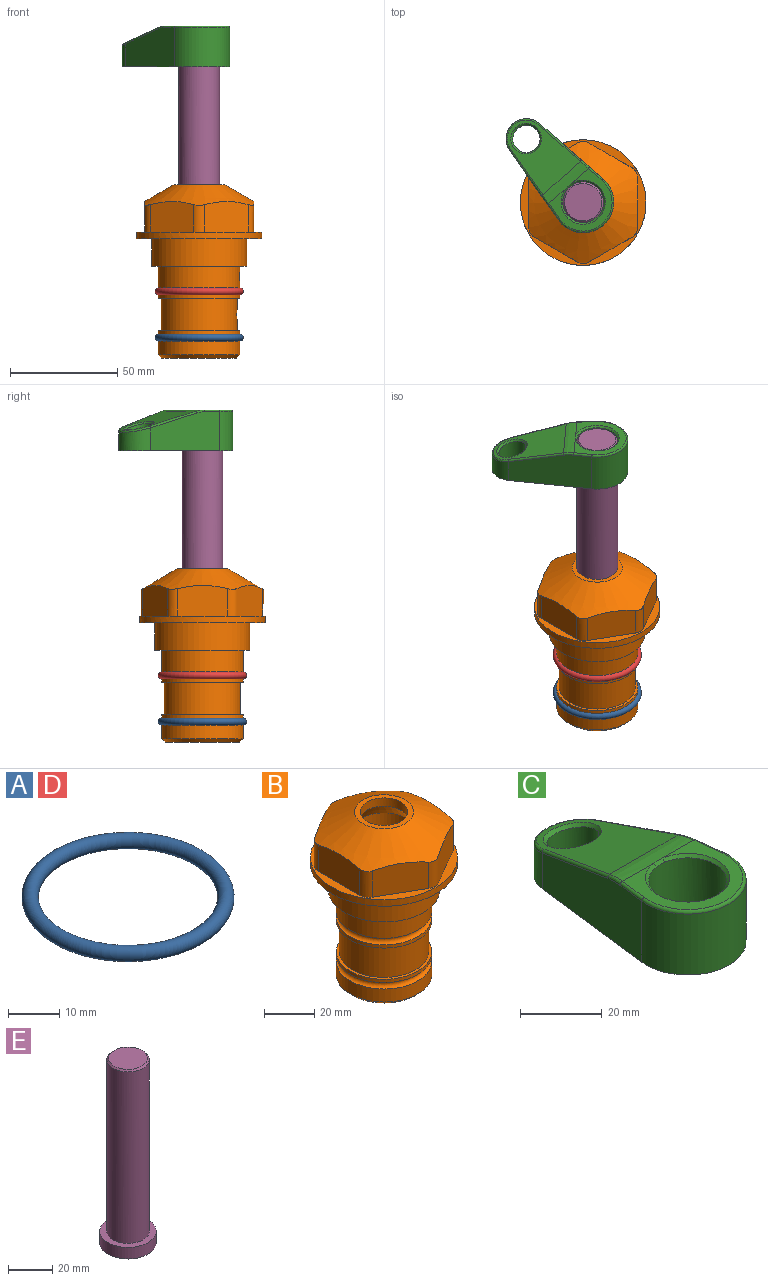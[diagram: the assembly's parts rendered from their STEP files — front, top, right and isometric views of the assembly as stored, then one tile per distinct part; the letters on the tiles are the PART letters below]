
ASSEMBLY  parts=5 mates=4
PART A: 1 faces, bbox 44.7x44.7x3.2 mm
  f0: torus R=19.05mm, axis (0,0,1), area 1193.9mm2
PART B: 36 faces, bbox 58.7x58.7x81 mm
  f0: cylinder r=17.78mm len=35.56mm, axis (0,0,1), area 1670.8mm2, adj f23,f24,f31
  f1: cylinder r=19.05mm len=38.1mm, axis (0,0,1), area 1191.9mm2, adj f26,f27,f30
  f2: plane 58.66x58.66mm, normal (0,0,-1), area 1150.6mm2, adj f3,f28
  f3: cylinder r=29.33mm len=58.66mm, axis (0,0,-1), area 585.1mm2, adj f2,f4
  f4: plane 58.66x58.66mm, normal (0,0,1), area 475.9mm2, adj f3,f5,f6,f7,f8,f9,f10,f11
  f5: plane 20.32x14.34mm, normal (-0.5,0.87,0), area 324.4mm2, adj f4,f15,f16,f17
  f6: plane 20.32x14.34mm, normal (0.5,0.87,0), area 324.4mm2, adj f4,f14,f15,f17
  f7: plane 23.48x14.34mm, normal (1,0,0), area 324.4mm2, adj f4,f13,f14,f17
  f8: plane 20.32x14.34mm, normal (0.5,-0.87,0), area 324.4mm2, adj f4,f12,f13,f17
  f9: plane 20.32x14.34mm, normal (-0.5,-0.87,0), area 324.4mm2, adj f4,f11,f12,f17
  f10: plane 23.48x14.34mm, normal (-1,0,0), area 324.4mm2, adj f4,f11,f16,f17
  f11: cylinder r=5.08mm len=12.85mm, axis (0,0,-1), area 67.2mm2, adj f4,f9,f10,f17
  f12: cylinder r=5.08mm len=12.85mm, axis (0,0,-1), area 67.2mm2, adj f4,f8,f9,f17
  f13: cylinder r=5.08mm len=12.85mm, axis (0,0,-1), area 67.2mm2, adj f4,f7,f8,f17
  f14: cylinder r=5.08mm len=12.85mm, axis (0,0,-1), area 67.2mm2, adj f4,f6,f7,f17
  f15: cylinder r=5.08mm len=12.85mm, axis (0,0,-1), area 67.2mm2, adj f4,f5,f6,f17
  f16: cylinder r=5.08mm len=12.85mm, axis (0,0,-1), area 67.2mm2, adj f4,f5,f10,f17
  f17: cone r=11.73mm half-angle=60deg, axis (0,0,-1), area 2071.8mm2, adj f5,f6,f7,f8,f9,f10,f11,f12
  f18: plane 23.46x23.46mm, normal (0,0,1), area 147.4mm2, adj f17,f35
  f19: plane 34.93x34.93mm, normal (0,0,-1), area 958mm2, adj f29
  f20: cylinder r=19.05mm len=38.1mm, axis (0,0,1), area 760.1mm2, adj f21,f29
  f21: torus R=19.05mm, axis (0,0,1), area 565.3mm2, adj f20,f22
  f22: cylinder r=19.05mm len=38.1mm, axis (0,0,1), area 190mm2, adj f21,f23
  f23: plane 38.1x38.1mm, normal (0,0,1), area 146.9mm2, adj f0,f22
  f24: plane 38.1x38.1mm, normal (0,0,-1), area 146.9mm2, adj f0,f25
  f25: cylinder r=19.05mm len=38.1mm, axis (0,0,1), area 190mm2, adj f24,f26
  f26: torus R=19.05mm, axis (0,0,1), area 565.3mm2, adj f1,f25
  f27: plane 44.45x44.45mm, normal (0,0,-1), area 411.7mm2, adj f1,f28
  f28: cylinder r=22.23mm len=44.45mm, axis (0,0,1), area 1773.5mm2, adj f2,f27
  f29: cone r=19.05mm half-angle=45deg, axis (0,0,1), area 257.5mm2, adj f19,f20
  f30: cylinder r=3.17mm len=6.75mm, axis (-1,0,0), area 128mm2, adj f1,f33
  f31: cylinder r=3.17mm len=6.35mm, axis (-1,0,0), area 102.5mm2, adj f0,f33
  f32: plane 25.4x25.4mm, normal (0,0,1), area 506.7mm2, adj f33
  f33: cylinder r=12.7mm len=66.42mm, axis (0,0,-1), area 5236.2mm2, adj f30,f31,f32,f34
  f34: cone r=9.53mm half-angle=30deg, axis (0,0,-1), area 443.4mm2, adj f33,f35
  f35: cylinder r=9.53mm len=19.05mm, axis (0,0,-1), area 240.9mm2, adj f18,f34
PART C: 31 faces, bbox 31.7x65.5x19.8 mm
  f0: plane 39.12x18.26mm, normal (0.99,0.12,0), area 612.2mm2, adj f1,f4,f7,f11,f13,f15
  f1: cylinder r=9.53mm len=18.91mm, axis (0,0,-1), area 296.1mm2, adj f0,f2,f7,f17
  f2: plane 39.12x18.26mm, normal (-0.99,0.12,0), area 612.2mm2, adj f1,f4,f7,f12,f14,f16
  f3: cylinder r=6.35mm len=12.7mm, axis (0,0,-1), area 362.4mm2, adj f7,f18
  f4: cylinder r=14.29mm len=28.58mm, axis (0,0,-1), area 882.2mm2, adj f0,f2,f7,f10
  f5: cylinder r=9.53mm len=19.05mm, axis (0,0,-1), area 1092.6mm2, adj f7,f19,f20
  f6: plane 26.99x23.69mm, normal (0,0,1), area 216.2mm2, adj f9,f10,f11,f12,f19
  f7: plane 63.5x28.58mm, normal (0,0,-1), area 661.8mm2, adj f0,f1,f2,f3,f4,f5,f22,f23
  f8: plane 33.52x23.6mm, normal (0,0.26,0.97), area 486mm2, adj f9,f15,f16,f17,f18
  f9: cylinder r=19.05mm len=24.72mm, axis (1,0,0), area 120.4mm2, adj f6,f8,f13,f14,f20
  f10: torus R=13.49mm, axis (0,0,1), area 59mm2, adj f4,f6,f11,f12
  f11: cylinder r=0.79mm len=8.67mm, axis (0.12,-0.99,0), area 10.8mm2, adj f0,f6,f10,f13
  f12: cylinder r=0.79mm len=8.67mm, axis (0.12,0.99,0), area 10.8mm2, adj f2,f6,f10,f14
  f13: bspline ~4.95x1.42mm, area 6.1mm2, adj f0,f9,f11,f15
  f14: bspline ~4.95x1.42mm, area 6.1mm2, adj f2,f9,f12,f16
  f15: cylinder r=0.79mm len=25.95mm, axis (0.12,-0.96,0.26), area 32.9mm2, adj f0,f8,f13,f17
  f16: cylinder r=0.79mm len=25.95mm, axis (0.12,0.96,-0.26), area 32.9mm2, adj f2,f8,f14,f17
  f17: bspline ~18.91x8.38mm, area 30mm2, adj f1,f8,f15,f16
  f18: bspline ~14.29x14.29mm, area 48.3mm2, adj f3,f8
  f19: cone r=9.53mm half-angle=45deg, axis (0,0,1), area 66.5mm2, adj f5,f6,f20
  f20: bspline ~3.22x0.96mm, area 3.5mm2, adj f5,f9,f19
  f21: plane 2.75x2.72mm, normal (0,0,-1), area 2.9mm2, adj f23,f25,f28
  f22: plane 23.05x15.88mm, normal (-0.99,-0.12,0), area 323.6mm2, adj f7,f25,f26,f27,f28,f29
  f23: plane 23.05x15.88mm, normal (0.99,-0.12,0), area 323.6mm2, adj f7,f21,f25,f27,f28,f30
  f24: cylinder r=9.53mm len=10.69mm, axis (0,0,-1), area 114.7mm2, adj f7,f27,f29,f30
  f25: cylinder r=12.7mm len=20.59mm, axis (0,0,-1), area 381.1mm2, adj f7,f21,f22,f23,f26,f28
  f26: plane 2.75x2.72mm, normal (0,0,-1), area 2.9mm2, adj f22,f25,f28
  f27: plane 19.72x18.37mm, normal (0,-0.26,-0.97), area 291.8mm2, adj f22,f23,f24,f28,f29,f30
  f28: cylinder r=15.88mm len=19.92mm, axis (1,0,0), area 54.8mm2, adj f21,f22,f23,f25,f26,f27
  f29: cylinder r=1.59mm len=11mm, axis (0,0,-1), area 34.7mm2, adj f7,f22,f24,f27
  f30: cylinder r=1.59mm len=11mm, axis (0,0,-1), area 34.7mm2, adj f7,f23,f24,f27
PART D: same geometry as A
PART E: 6 faces, bbox 25.4x25.4x101.6 mm
  f0: plane 17.46x17.46mm, normal (0,0,1), area 239.5mm2, adj f5
  f1: plane 25.4x25.4mm, normal (0,0,-1), area 506.7mm2, adj f2
  f2: cylinder r=12.7mm len=25.4mm, axis (0,0,1), area 506.7mm2, adj f1,f3
  f3: plane 25.4x25.4mm, normal (0,0,1), area 221.7mm2, adj f2,f4
  f4: cylinder r=9.53mm len=94.46mm, axis (0,0,1), area 5653mm2, adj f3,f5
  f5: cone r=8.73mm half-angle=45deg, axis (0,0,-1), area 64.4mm2, adj f0,f4
PLACE A t=(0,0,-21.59)mm
PLACE B at identity fixed
PLACE C rot(axis=(0,0,1),41.9deg) t=(0,0,35.97)mm
PLACE D at identity
PLACE E rot(axis=(0,0,1),41.9deg) t=(0,0,35.17)mm
MATE fastened D.f0 <-> B.f0  axis (0,0,1) through (0,0,-24.51)mm
MATE cylindrical E.f2 <-> B.f0  axis (0,0,-1) through (0,0,-2.93)mm
MATE fastened E.f2 <-> C.f4  axis (0,0,1) through (0,0,98.67)mm
MATE fastened A.f0 <-> B.f0  axis (0,0,1) through (0,0,-46.1)mm
